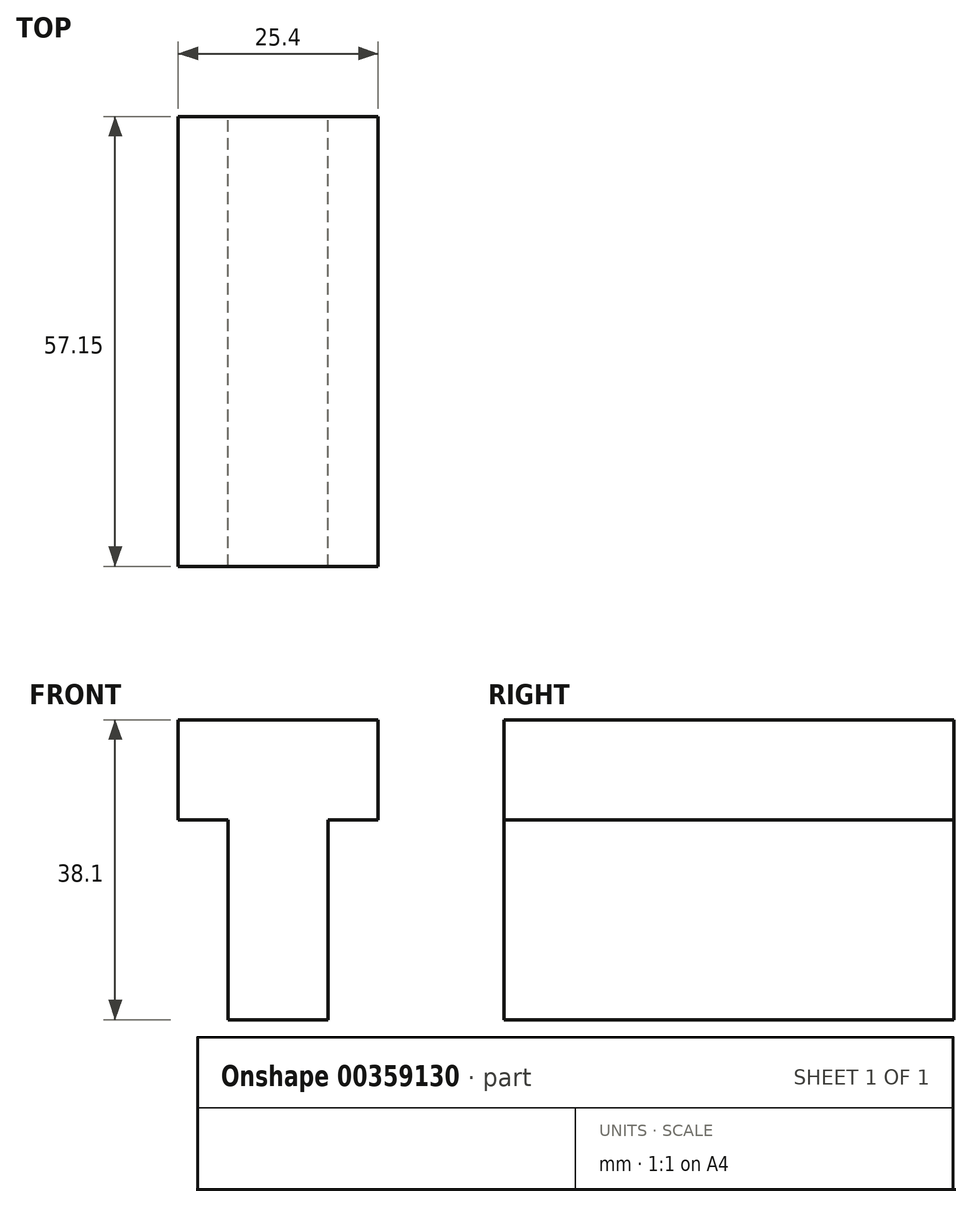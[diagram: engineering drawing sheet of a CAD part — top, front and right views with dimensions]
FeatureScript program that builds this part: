
annotation { "Feature Type Name" : "Feature", "Feature Type Description" : "" }
export const myFeature = defineFeature(function(context is Context, id is Id, definition is map)
    precondition{}
    {
        {
            var Q0;
            Q0=qCreatedBy(makeId("Front.planeOp"),FACE);
            var sketch = newSketch(context, id + "F0", { "sketchPlane" : qUnion([Q0])});
            skLineSegment(sketch, "E0", {"start": v(-19.05, 14.62) * mm, "end": v(6.35, 14.62) * mm});
            skLineSegment(sketch, "E1", {"start": v(6.35, 14.62) * mm, "end": v(6.35, 1.92) * mm});
            skLineSegment(sketch, "E2", {"start": v(6.35, 1.92) * mm, "end": v(0, 1.92) * mm});
            skLineSegment(sketch, "E3", {"start": v(0, 1.92) * mm, "end": v(0, -23.48) * mm});
            skLineSegment(sketch, "E4", {"start": v(0, -23.48) * mm, "end": v(-12.7, -23.48) * mm});
            skLineSegment(sketch, "E5", {"start": v(-12.7, -23.48) * mm, "end": v(-12.7, 1.92) * mm});
            skLineSegment(sketch, "E6", {"start": v(-12.7, 1.92) * mm, "end": v(-19.05, 1.92) * mm});
            skLineSegment(sketch, "E7", {"start": v(-19.05, 1.92) * mm, "end": v(-19.05, 14.62) * mm});
            skSolve(sketch);
        }
        {
            var Q0;
            Q0=makeQuery(id+"F0.imprint","IMPRINT",FACE,{"disambiguationData":[TD([[makeQuery(id+"F0.imprint","IMPRINT",EDGE,{"derivedFrom":sQuery(id+"F0.wireOp",EDGE,"E0")}),-1.0]])]});
            var Q1;
            Q1 = qSketchRegion(id + "F0", true);
            extrude(context, id + "F1", {"entities" : qUnion([Q0, Q1]), "depth" : 25.4 * mm});
        }
        {
            var Q0;
            Q0=makeQuery(id+"F1.opExtrude","CAP_FACE",FACE,{"disambiguationData":[OSD([sQuery(id+"F0.wireOp",EDGE,"E0"),sQuery(id+"F0.wireOp",EDGE,"E1"),sQuery(id+"F0.wireOp",EDGE,"E2"),sQuery(id+"F0.wireOp",EDGE,"E3"),sQuery(id+"F0.wireOp",EDGE,"E4"),sQuery(id+"F0.wireOp",EDGE,"E5"),sQuery(id+"F0.wireOp",EDGE,"E6"),sQuery(id+"F0.wireOp",EDGE,"E7")])],"isStart":false});
            extrude(context, id + "F2", {"entities" : qUnion([Q0]), "operationType" : NewBodyOperationType.ADD, "depth" : 31.75 * mm});
        }
    });
